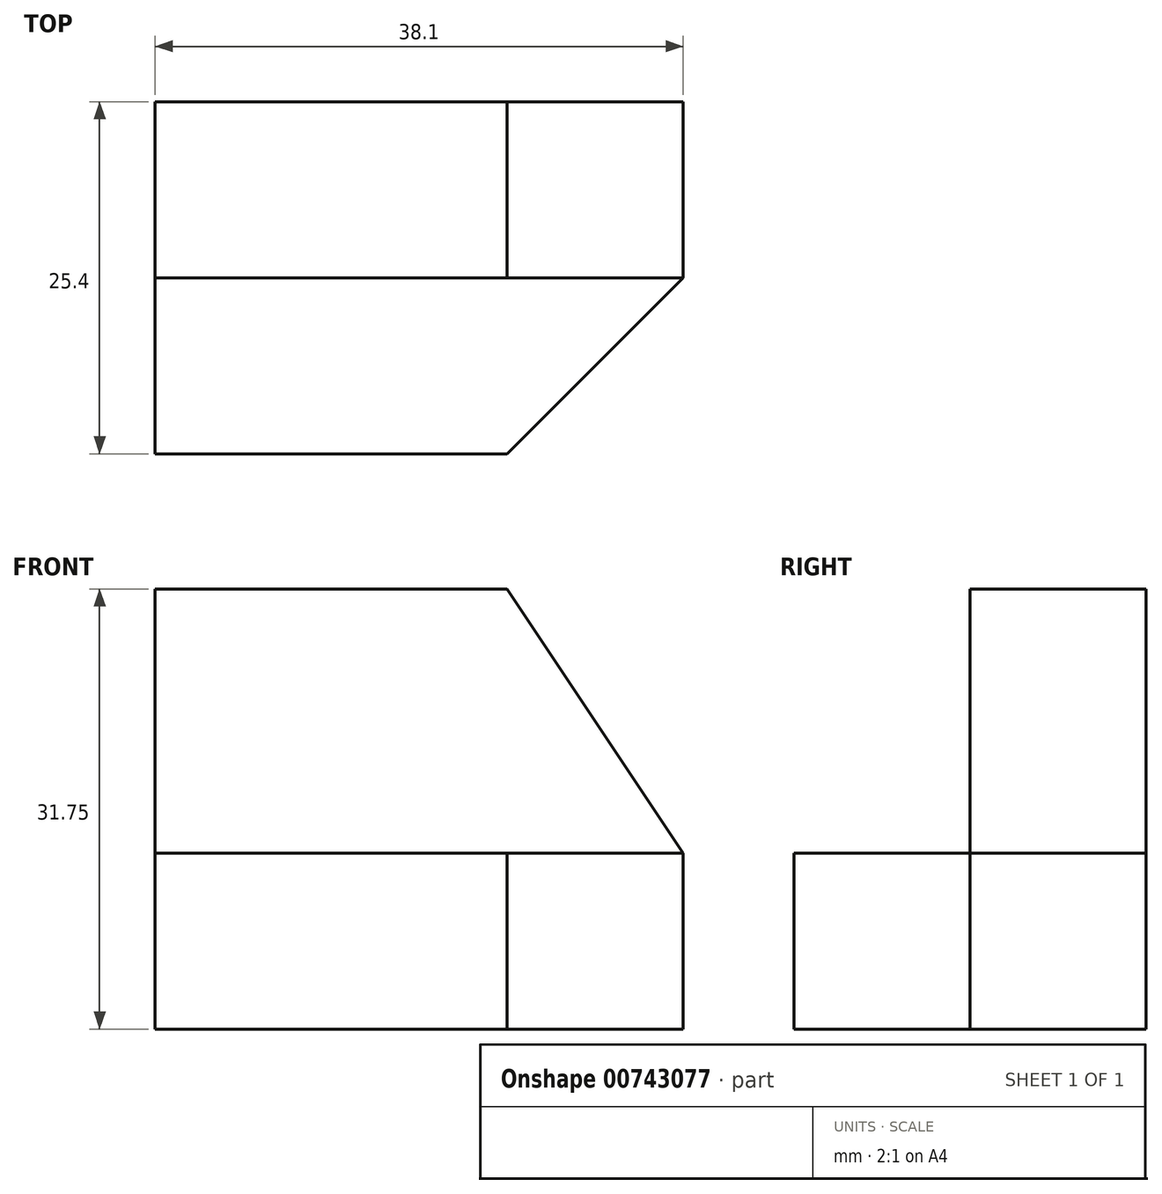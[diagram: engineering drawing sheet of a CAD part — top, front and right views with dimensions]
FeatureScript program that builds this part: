
annotation { "Feature Type Name" : "Feature", "Feature Type Description" : "" }
export const myFeature = defineFeature(function(context is Context, id is Id, definition is map)
    precondition{}
    {
        {
            var Q0;
            Q0=qCreatedBy(makeId("Front.planeOp"),FACE);
            var sketch = newSketch(context, id + "F0", { "sketchPlane" : qUnion([Q0])});
            skLineSegment(sketch, "E0", {"start": v(0, 0) * mm, "end": v(38.1, 0) * mm});
            skLineSegment(sketch, "E1", {"start": v(38.1, 0) * mm, "end": v(38.1, 31.75) * mm});
            skLineSegment(sketch, "E2", {"start": v(38.1, 31.75) * mm, "end": v(0, 31.75) * mm});
            skLineSegment(sketch, "E3", {"start": v(0, 31.75) * mm, "end": v(0, 0) * mm});
            skSolve(sketch);
        }
        {
            var Q0;
            Q0=makeQuery(id+"F0.imprint","IMPRINT",FACE,{"disambiguationData":[TD([[makeQuery(id+"F0.imprint","IMPRINT",EDGE,{"derivedFrom":sQuery(id+"F0.wireOp",EDGE,"E0")}),1.0]])]});
            extrude(context, id + "F1", {"entities" : qUnion([Q0]), "depth" : 25.4 * mm, "offsetDistance" : 25.4 * mm});
        }
        {
            var Q0;
            Q0=makeQuery(id+"F1.opExtrude","SWEPT_FACE",FACE,{"disambiguationData":[OSD([sQuery(id+"F0.wireOp",EDGE,"E2")])]});
            var sketch = newSketch(context, id + "F2", { "sketchPlane" : qUnion([Q0])});
            skLineSegment(sketch, "E4", {"start": v(0, -12.7) * mm, "end": v(38.1, -12.7) * mm});
            skSolve(sketch);
        }
        {
            var Q0;
            {var subQ0=sQuery(id+"F2.wireOp",EDGE,"E4");Q0=makeQuery(id+"F2.imprint","IMPRINT",FACE,{"disambiguationData":[TD([[makeQuery(id+"F2.imprint","IMPRINT",EDGE,{"derivedFrom":subQ0}),-1.0]])]});}
            extrude(context, id + "F3", {"entities" : qUnion([Q0]), "operationType" : NewBodyOperationType.REMOVE, "oppositeDirection" : true, "depth" : 19.05 * mm, "offsetDistance" : 25.4 * mm});
        }
        {
            var Q0;
            Q0=makeQuery(id+"F3.boolean.opBoolean","COPY",FACE,{"derivedFrom":makeQuery(id+"F3.opExtrude","SWEPT_FACE",FACE,{"disambiguationData":[OSD([sQuery(id+"F2.wireOp",EDGE,"E4")])]})});
            var sketch = newSketch(context, id + "F4", { "sketchPlane" : qUnion([Q0])});
            skLineSegment(sketch, "E5", {"start": v(25.4, 31.75) * mm, "end": v(38.1, 12.7) * mm});
            skSolve(sketch);
        }
        {
            var Q0;
            {var subQ0=sQuery(id+"F4.wireOp",EDGE,"E5");Q0=makeQuery(id+"F4.imprint","IMPRINT",FACE,{"disambiguationData":[TD([[makeQuery(id+"F4.imprint","IMPRINT",EDGE,{"derivedFrom":subQ0}),1.0]])]});}
            extrude(context, id + "F5", {"entities" : qUnion([Q0]), "operationType" : NewBodyOperationType.REMOVE, "oppositeDirection" : true, "depth" : 12.7 * mm, "offsetDistance" : 25.4 * mm});
        }
        {
            var Q0;
            Q0=makeQuery(id+"F1.opExtrude","CAP_FACE",FACE,{"disambiguationData":[OSD([sQuery(id+"F0.wireOp",EDGE,"E0"),sQuery(id+"F0.wireOp",EDGE,"E1"),sQuery(id+"F0.wireOp",EDGE,"E2"),sQuery(id+"F0.wireOp",EDGE,"E3")])],"isStart":false});
            var sketch = newSketch(context, id + "F6", { "sketchPlane" : qUnion([Q0])});
            skLineSegment(sketch, "E6", {"start": v(38.1, 12.7) * mm, "end": v(25.4, 0) * mm});
            skSolve(sketch);
        }
        {
            var Q0;
            {var subQ0=sQuery(id+"F6.wireOp",EDGE,"E6");Q0=makeQuery(id+"F6.imprint","IMPRINT",FACE,{"disambiguationData":[TD([[makeQuery(id+"F6.imprint","IMPRINT",EDGE,{"derivedFrom":subQ0}),1.0]])]});}
            extrude(context, id + "F7", {"entities" : qUnion([Q0]), "operationType" : NewBodyOperationType.ADD, "depth" : 38.1 * mm, "offsetDistance" : 25.4 * mm});
        }
        {
            var Q0;
            Q0=makeQuery(id+"F7.opExtrude","SWEPT_FACE",FACE,{"disambiguationData":[OSD([sQuery(id+"F6.wireOp",EDGE,"E6")])]});
            extrude(context, id + "F8", {"entities" : qUnion([Q0]), "operationType" : NewBodyOperationType.REMOVE, "oppositeDirection" : true, "depth" : 25.4 * mm, "offsetDistance" : 25.4 * mm});
        }
        {
            var Q0;
            Q0=makeQuery(id+"F3.boolean.opBoolean","COPY",FACE,{"derivedFrom":makeQuery(id+"F3.opExtrude","CAP_FACE",FACE,{"disambiguationData":[OSD([sQuery(id+"F0.wireOp",EDGE,"E1"),sQuery(id+"F0.wireOp",EDGE,"E2"),sQuery(id+"F0.wireOp",EDGE,"E3"),sQuery(id+"F2.wireOp",EDGE,"E4")])],"isStart":false})});
            var sketch = newSketch(context, id + "F9", { "sketchPlane" : qUnion([Q0])});
            skLineSegment(sketch, "E7", {"start": v(38.1, -12.7) * mm, "end": v(25.4, -25.4) * mm});
            skSolve(sketch);
        }
        {
            var Q0;
            {var subQ0=sQuery(id+"F9.wireOp",EDGE,"E7");Q0=makeQuery(id+"F9.imprint","IMPRINT",FACE,{"disambiguationData":[TD([[makeQuery(id+"F9.imprint","IMPRINT",EDGE,{"derivedFrom":subQ0}),1.0]])]});}
            extrude(context, id + "F10", {"entities" : qUnion([Q0]), "operationType" : NewBodyOperationType.REMOVE, "oppositeDirection" : true, "depth" : 12.7 * mm, "offsetDistance" : 25.4 * mm});
        }
    });
